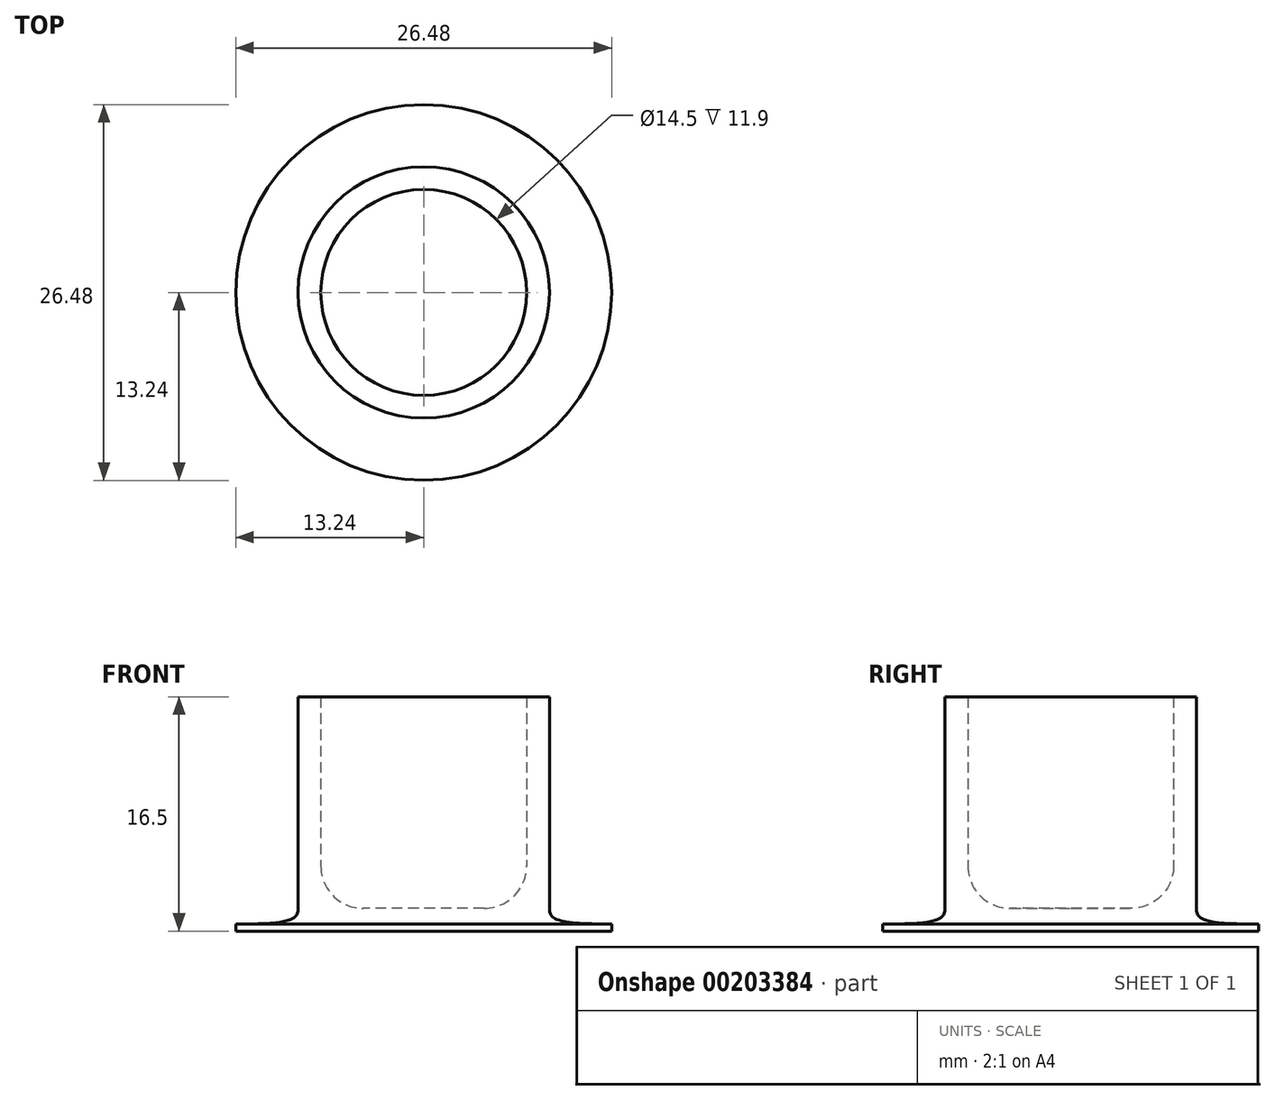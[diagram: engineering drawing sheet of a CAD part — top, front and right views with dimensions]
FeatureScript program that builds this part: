
annotation { "Feature Type Name" : "Feature", "Feature Type Description" : "" }
export const myFeature = defineFeature(function(context is Context, id is Id, definition is map)
    precondition{}
    {
        {
            var Q0;
            Q0=qCreatedBy(makeId("Top.planeOp"),FACE);
            var sketch = newSketch(context, id + "F0", { "sketchPlane" : qUnion([Q0])});
            skCircle(sketch, "E0", {"center": v(0, 0) * mm, "radius": 7.25 * mm});
            skCircle(sketch, "E1.0", {"center": v(0, 0) * mm, "radius": 8.85 * mm});
            skSolve(sketch);
        }
        {
            var Q0;
            Q0=makeQuery(id+"F0.imprint","IMPRINT",FACE,{"disambiguationData":[TD([[makeQuery(id+"F0.imprint","IMPRINT",EDGE,{"derivedFrom":sQuery(id+"F0.wireOp",EDGE,"E0")}),-1.0]])]});
            extrude(context, id + "F1", {"entities" : qUnion([Q0]), "depth" : 15 * mm});
        }
        {
            var Q0;
            Q0=makeQuery(id+"F0.imprint","IMPRINT",FACE,{"disambiguationData":[TD([[makeQuery(id+"F0.imprint","IMPRINT",EDGE,{"derivedFrom":sQuery(id+"F0.wireOp",EDGE,"E0")}),1.0]])]});
            var Q1;
            Q1=makeQuery(id+"F0.imprint","IMPRINT",FACE,{"disambiguationData":[TD([[makeQuery(id+"F0.imprint","IMPRINT",EDGE,{"derivedFrom":sQuery(id+"F0.wireOp",EDGE,"E0")}),-1.0]])]});
            extrude(context, id + "F2", {"entities" : qUnion([Q0, Q1]), "operationType" : NewBodyOperationType.ADD, "depth" : 0.1 * mm});
        }
        {
            var Q0;
            Q0=makeQuery(id+"F2.opExtrude","CAP_FACE",FACE,{"disambiguationData":[OSD([sQuery(id+"F0.wireOp",EDGE,"E1.0")])],"isStart":true});
            cPlane(context, id + "F3", {"entities" : qUnion([Q0]), "cplaneType" : CPlaneType.OFFSET, "offset" : 1 * mm, "width" : 150 * mm, "height" : 150 * mm});
        }
        {
            var Q0;
            Q0=qCreatedBy(id+"F3.planeOp",FACE);
            var sketch = newSketch(context, id + "F4", { "sketchPlane" : qUnion([Q0])});
            skCircle(sketch, "E2", {"center": v(0, 0) * mm, "radius": 13.24 * mm});
            skSolve(sketch);
        }
        {
            var Q1;
            {var subQ0=sQuery(id+"F0.wireOp",EDGE,"E1.0");Q1=makeQuery(id+"F2.boolean.opBoolean","MERGE",FACE,{"derivedFrom":[makeQuery(id+"F1.opExtrude","CAP_FACE",FACE,{"disambiguationData":[OSD([sQuery(id+"F0.wireOp",EDGE,"E0"),subQ0])],"isStart":true}),makeQuery(id+"F2.opExtrude","CAP_FACE",FACE,{"disambiguationData":[OSD([subQ0])],"isStart":true})]});}
            var Q2;
            Q2=makeQuery(id+"F4.imprint","IMPRINT",FACE,{"disambiguationData":[TD([[makeQuery(id+"F4.imprint","IMPRINT",EDGE,{"derivedFrom":sQuery(id+"F4.wireOp",EDGE,"E2")}),1.0]])]});
            loft(context, id + "F5", {"operationType" : NewBodyOperationType.ADD, "startCondition" : LoftEndDerivativeType.NORMAL_TO_PROFILE, "startMagnitude" : 2, "endCondition" : LoftEndDerivativeType.TANGENT_TO_PROFILE, "endMagnitude" : 2, "sheetProfilesArray" : [{ "sheetProfileEntities" : qUnion([Q1]) }, { "sheetProfileEntities" : qUnion([Q2]) }]});
        }
        {
            var Q0;
            Q0=makeQuery(id+"F5.opLoft","CAP_FACE",FACE,{"disambiguationData":[OSD([makeQuery(id+"F4.imprint","IMPRINT",FACE,{"disambiguationData":[TD([[makeQuery(id+"F4.imprint","IMPRINT",EDGE,{"derivedFrom":sQuery(id+"F4.wireOp",EDGE,"E2")}),1.0]])]})])],"isStart":true});
            extrude(context, id + "F6", {"entities" : qUnion([Q0]), "operationType" : NewBodyOperationType.ADD, "depth" : 0.5 * mm});
        }
        {
            var Q0;
            Q0=makeQuery(id+"F2.boolean.opBoolean","INTERSECT",EDGE,{"derivedFrom":[makeQuery(id+"F1.opExtrude","SWEPT_FACE",FACE,{"disambiguationData":[OSD([sQuery(id+"F0.wireOp",EDGE,"E0")])]}),makeQuery(id+"F2.opExtrude","CAP_FACE",FACE,{"disambiguationData":[OSD([sQuery(id+"F0.wireOp",EDGE,"E1.0")])],"isStart":false})]});
            fillet(context, id + "F7", {"entities" : qUnion([Q0]), "radius" : 3 * mm, "tangentPropagation" : true, "allowEdgeOverflow" : false});
        }
    });
